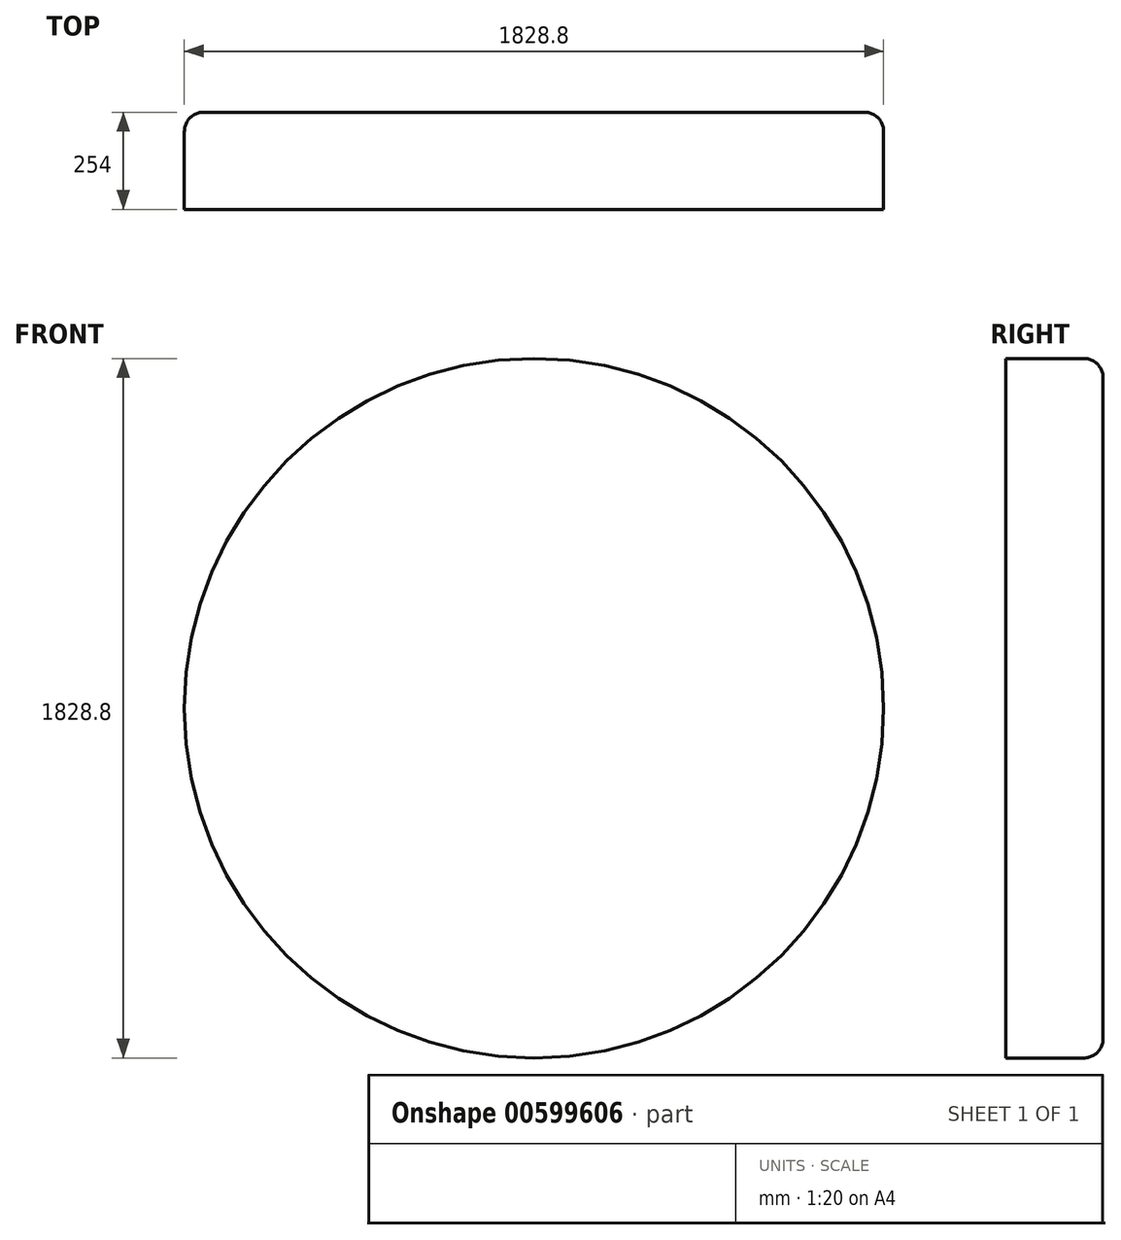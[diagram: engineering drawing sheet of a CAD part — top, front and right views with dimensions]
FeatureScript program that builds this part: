
annotation { "Feature Type Name" : "Feature", "Feature Type Description" : "" }
export const myFeature = defineFeature(function(context is Context, id is Id, definition is map)
    precondition{}
    {
        {
            var Q0;
            Q0=qCreatedBy(makeId("Front.planeOp"),FACE);
            var sketch = newSketch(context, id + "F0", { "sketchPlane" : qUnion([Q0])});
            skCircle(sketch, "E0", {"center": v(0, 0) * mm, "radius": 914.4 * mm});
            skSolve(sketch);
        }
        {
            var Q0;
            Q0 = qSketchRegion(id + "F0", true);
            extrude(context, id + "F1", {"entities" : qUnion([Q0]), "oppositeDirection" : true, "depth" : 254 * mm, "offsetDistance" : 25.4 * mm});
        }
        {
            var Q0;
            Q0=makeQuery(id+"F1.opExtrude","CAP_EDGE",EDGE,{"disambiguationData":[OSD([sQuery(id+"F0.wireOp",EDGE,"E0")])],"isStart":false});
            fillet(context, id + "F2", {"entities" : qUnion([Q0]), "radius" : 50.8 * mm, "tangentPropagation" : true, "allowEdgeOverflow" : false});
        }
        {
            var Q0;
            Q0=makeQuery(id+"F1.opExtrude","CAP_FACE",FACE,{"disambiguationData":[OSD([sQuery(id+"F0.wireOp",EDGE,"E0")])],"isStart":true});
            var sketch = newSketch(context, id + "F3", { "sketchPlane" : qUnion([Q0])});
            skCircle(sketch, "E1", {"center": v(0, 0) * mm, "radius": 127 * mm});
            skSolve(sketch);
        }
        {
            var Q0;
            Q0=sQuery(id+"F3.wireOp",EDGE,"E1");
            extrude(context, id + "F4", {"bodyType" : ToolBodyType.SURFACE, "operationType" : NewBodyOperationType.REMOVE, "surfaceEntities" : qUnion([Q0]), "depth" : 152.4 * mm, "offsetDistance" : 25.4 * mm});
        }
    });
